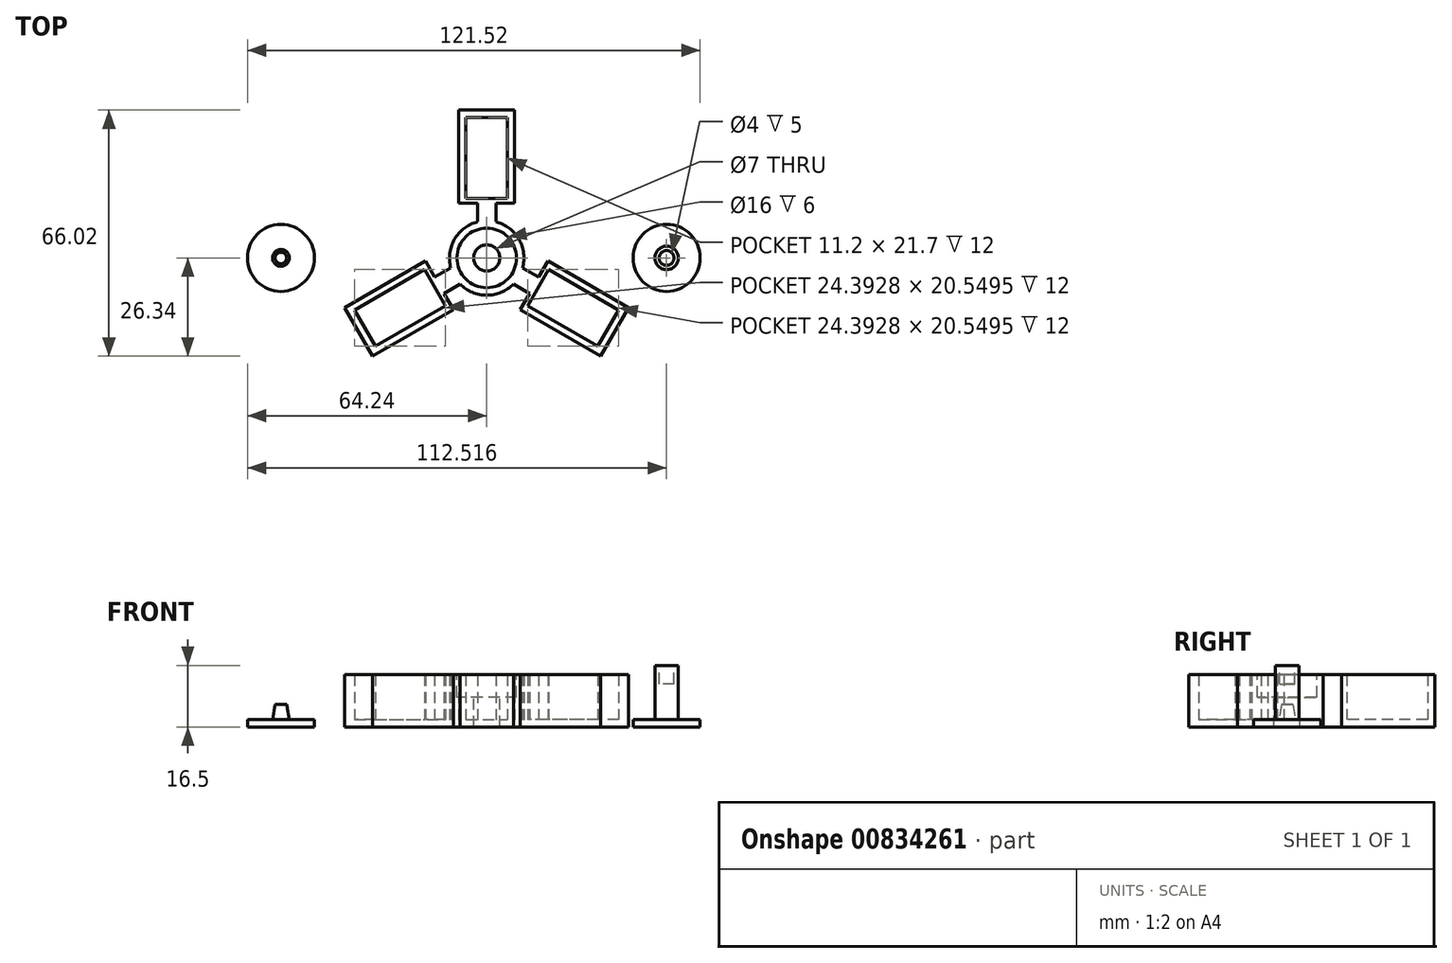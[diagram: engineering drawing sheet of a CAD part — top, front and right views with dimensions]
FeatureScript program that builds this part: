
annotation { "Feature Type Name" : "Feature", "Feature Type Description" : "" }
export const myFeature = defineFeature(function(context is Context, id is Id, definition is map)
    precondition{}
    {
        {
            var Q0;
            Q0=qCreatedBy(makeId("Top.planeOp"),FACE);
            var sketch = newSketch(context, id + "F0", { "sketchPlane" : qUnion([Q0])});
            skCircle(sketch, "E0", {"center": v(0, 0) * mm, "radius": 10 * mm});
            skPoint(sketch, "E1", {"position": v(-2.5, 9.68) * mm});
            skPoint(sketch, "E2", {"position": v(2.5, 9.68) * mm});
            skLineSegment(sketch, "E3", {"start": v(0, 24.16) * mm, "end": v(0, -23.06) * mm, "construction": true});
            skLineSegment(sketch, "E4", {"start": v(-2.5, 9.68) * mm, "end": v(-2.5, 14.68) * mm});
            skLineSegment(sketch, "E5", {"start": v(-2.5, 14.68) * mm, "end": v(2.5, 14.68) * mm});
            skLineSegment(sketch, "E6", {"start": v(2.5, 14.68) * mm, "end": v(2.5, 9.68) * mm});
            skLineSegment(sketch, "E7.bottom", {"start": v(-7.5, 14.68) * mm, "end": v(7.5, 14.68) * mm});
            skLineSegment(sketch, "E7.top", {"start": v(-7.5, 39.68) * mm, "end": v(7.5, 39.68) * mm});
            skLineSegment(sketch, "E7.left", {"start": v(-7.5, 14.68) * mm, "end": v(-7.5, 39.68) * mm});
            skLineSegment(sketch, "E7.right", {"start": v(7.5, 14.68) * mm, "end": v(7.5, 39.68) * mm});
            skLineSegment(sketch, "E8.1.0", {"start": v(-8.97, -13.84) * mm, "end": v(-30.62, -26.34) * mm});
            skLineSegment(sketch, "E8.1.1", {"start": v(-20.93, -12.08) * mm, "end": v(19.97, 11.53) * mm, "construction": true});
            skLineSegment(sketch, "E8.1.2", {"start": v(-16.47, -0.85) * mm, "end": v(-38.12, -13.35) * mm});
            skLineSegment(sketch, "E8.1.3", {"start": v(-7.14, -7) * mm, "end": v(-11.47, -9.5) * mm});
            skLineSegment(sketch, "E8.1.4", {"start": v(-13.97, -5.18) * mm, "end": v(-9.64, -2.68) * mm});
            skLineSegment(sketch, "E8.1.5", {"start": v(-8.97, -13.84) * mm, "end": v(-16.47, -0.85) * mm});
            skLineSegment(sketch, "E8.1.6", {"start": v(-30.62, -26.34) * mm, "end": v(-38.12, -13.35) * mm});
            skLineSegment(sketch, "E8.1.7", {"start": v(-11.47, -9.5) * mm, "end": v(-13.97, -5.18) * mm});
            skLineSegment(sketch, "E8.2.0", {"start": v(16.47, -0.85) * mm, "end": v(38.12, -13.35) * mm});
            skLineSegment(sketch, "E8.2.1", {"start": v(20.93, -12.08) * mm, "end": v(-19.97, 11.53) * mm, "construction": true});
            skLineSegment(sketch, "E8.2.2", {"start": v(8.97, -13.84) * mm, "end": v(30.62, -26.34) * mm});
            skLineSegment(sketch, "E8.2.3", {"start": v(9.64, -2.68) * mm, "end": v(13.97, -5.18) * mm});
            skLineSegment(sketch, "E8.2.4", {"start": v(11.47, -9.5) * mm, "end": v(7.14, -7) * mm});
            skLineSegment(sketch, "E8.2.5", {"start": v(16.47, -0.85) * mm, "end": v(8.97, -13.84) * mm});
            skLineSegment(sketch, "E8.2.6", {"start": v(38.12, -13.35) * mm, "end": v(30.62, -26.34) * mm});
            skLineSegment(sketch, "E8.2.7", {"start": v(13.97, -5.18) * mm, "end": v(11.47, -9.5) * mm});
            skSolve(sketch);
        }
        {
            var Q0;
            Q0 = qSketchRegion(id + "F0", true);
            extrude(context, id + "F1", {"entities" : qUnion([Q0]), "depth" : 2 * mm, "offsetDistance" : 25 * mm});
        }
        {
            var Q0;
            Q0=makeQuery(id+"F1.opExtrude","CAP_FACE",FACE,{"disambiguationData":[OSD([sQuery(id+"F0.wireOp",EDGE,"E0"),sQuery(id+"F0.wireOp",EDGE,"E4"),sQuery(id+"F0.wireOp",EDGE,"E6"),sQuery(id+"F0.wireOp",EDGE,"E7.bottom"),sQuery(id+"F0.wireOp",EDGE,"E7.top"),sQuery(id+"F0.wireOp",EDGE,"E7.left"),sQuery(id+"F0.wireOp",EDGE,"E7.right"),sQuery(id+"F0.wireOp",EDGE,"E8.1.0"),sQuery(id+"F0.wireOp",EDGE,"E8.1.2"),sQuery(id+"F0.wireOp",EDGE,"E8.1.3"),sQuery(id+"F0.wireOp",EDGE,"E8.1.4"),sQuery(id+"F0.wireOp",EDGE,"E8.1.5"),sQuery(id+"F0.wireOp",EDGE,"E8.1.6"),sQuery(id+"F0.wireOp",EDGE,"E8.2.0"),sQuery(id+"F0.wireOp",EDGE,"E8.2.2"),sQuery(id+"F0.wireOp",EDGE,"E8.2.3"),sQuery(id+"F0.wireOp",EDGE,"E8.2.4"),sQuery(id+"F0.wireOp",EDGE,"E8.2.5"),sQuery(id+"F0.wireOp",EDGE,"E8.2.6")])],"isStart":false});
            var sketch = newSketch(context, id + "F2", { "sketchPlane" : qUnion([Q0])});
            skLineSegment(sketch, "E9", {"start": v(0, -5.79) * mm, "end": v(0, 41.24) * mm, "construction": true});
            skPoint(sketch, "E9.endSnap0", {"position": v(0, 39.68) * mm});
            skLineSegment(sketch, "E10.bottom", {"start": v(-5.6, 37.68) * mm, "end": v(5.6, 37.68) * mm});
            skLineSegment(sketch, "E10.top", {"start": v(-5.6, 15.98) * mm, "end": v(5.6, 15.98) * mm});
            skLineSegment(sketch, "E10.left", {"start": v(-5.6, 37.68) * mm, "end": v(-5.6, 15.98) * mm});
            skLineSegment(sketch, "E10.right", {"start": v(5.6, 37.68) * mm, "end": v(5.6, 15.98) * mm});
            skPoint(sketch, "E11.1.0", {"position": v(-34.37, -19.84) * mm});
            skLineSegment(sketch, "E11.1.1", {"start": v(-35.43, -14) * mm, "end": v(-16.64, -3.14) * mm});
            skLineSegment(sketch, "E11.1.2", {"start": v(-29.83, -23.7) * mm, "end": v(-11.04, -12.84) * mm});
            skLineSegment(sketch, "E11.1.3", {"start": v(-11.04, -12.84) * mm, "end": v(-16.64, -3.14) * mm});
            skLineSegment(sketch, "E11.1.4", {"start": v(-29.83, -23.7) * mm, "end": v(-35.43, -14) * mm});
            skPoint(sketch, "E11.2.0", {"position": v(34.37, -19.84) * mm});
            skLineSegment(sketch, "E11.2.1", {"start": v(29.83, -23.7) * mm, "end": v(11.04, -12.84) * mm});
            skLineSegment(sketch, "E11.2.2", {"start": v(35.43, -14) * mm, "end": v(16.64, -3.14) * mm});
            skLineSegment(sketch, "E11.2.3", {"start": v(16.64, -3.14) * mm, "end": v(11.04, -12.84) * mm});
            skLineSegment(sketch, "E11.2.4", {"start": v(35.43, -14) * mm, "end": v(29.83, -23.7) * mm});
            skPoint(sketch, "E11.center", {"position": v(0, 0) * mm});
            skSolve(sketch);
        }
        {
            var Q0;
            Q0=makeQuery(id+"F2.imprint","IMPRINT",FACE,{"disambiguationData":[TD([[makeQuery(id+"F2.imprint","IMPRINT",EDGE,{"derivedFrom":sQuery(id+"F2.wireOp",EDGE,"E10.bottom")}),1.0]])]});
            extrude(context, id + "F3", {"entities" : qUnion([Q0]), "operationType" : NewBodyOperationType.ADD, "depth" : 12 * mm, "offsetDistance" : 25 * mm});
        }
        {
            var Q0;
            Q0=makeQuery(id+"F3.opExtrude","CAP_FACE",FACE,{"disambiguationData":[OSD([sQuery(id+"F0.wireOp",EDGE,"E0"),sQuery(id+"F0.wireOp",EDGE,"E4"),sQuery(id+"F0.wireOp",EDGE,"E6"),sQuery(id+"F0.wireOp",EDGE,"E7.bottom"),sQuery(id+"F0.wireOp",EDGE,"E7.top"),sQuery(id+"F0.wireOp",EDGE,"E7.left"),sQuery(id+"F0.wireOp",EDGE,"E7.right"),sQuery(id+"F0.wireOp",EDGE,"E8.1.0"),sQuery(id+"F0.wireOp",EDGE,"E8.1.2"),sQuery(id+"F0.wireOp",EDGE,"E8.1.3"),sQuery(id+"F0.wireOp",EDGE,"E8.1.4"),sQuery(id+"F0.wireOp",EDGE,"E8.1.5"),sQuery(id+"F0.wireOp",EDGE,"E8.1.6"),sQuery(id+"F0.wireOp",EDGE,"E8.2.0"),sQuery(id+"F0.wireOp",EDGE,"E8.2.2"),sQuery(id+"F0.wireOp",EDGE,"E8.2.3"),sQuery(id+"F0.wireOp",EDGE,"E8.2.4"),sQuery(id+"F0.wireOp",EDGE,"E8.2.5"),sQuery(id+"F0.wireOp",EDGE,"E8.2.6"),sQuery(id+"F2.wireOp",EDGE,"E10.bottom"),sQuery(id+"F2.wireOp",EDGE,"E10.top"),sQuery(id+"F2.wireOp",EDGE,"E10.left"),sQuery(id+"F2.wireOp",EDGE,"E10.right"),sQuery(id+"F2.wireOp",EDGE,"E11.1.1"),sQuery(id+"F2.wireOp",EDGE,"E11.1.2"),sQuery(id+"F2.wireOp",EDGE,"E11.1.3"),sQuery(id+"F2.wireOp",EDGE,"E11.1.4"),sQuery(id+"F2.wireOp",EDGE,"E11.2.1"),sQuery(id+"F2.wireOp",EDGE,"E11.2.2"),sQuery(id+"F2.wireOp",EDGE,"E11.2.3"),sQuery(id+"F2.wireOp",EDGE,"E11.2.4")])],"isStart":false});
            var sketch = newSketch(context, id + "F4", { "sketchPlane" : qUnion([Q0])});
            skCircle(sketch, "E12", {"center": v(0, 0) * mm, "radius": 3.5 * mm});
            skSolve(sketch);
        }
        {
            var Q0;
            Q0 = qSketchRegion(id + "F4", true);
            extrude(context, id + "F5", {"entities" : qUnion([Q0]), "operationType" : NewBodyOperationType.REMOVE, "oppositeDirection" : true, "depth" : 25 * mm, "offsetDistance" : 25 * mm});
        }
        {
            var Q0;
            Q0=makeQuery(id+"F3.opExtrude","CAP_FACE",FACE,{"disambiguationData":[OSD([sQuery(id+"F0.wireOp",EDGE,"E0"),sQuery(id+"F0.wireOp",EDGE,"E4"),sQuery(id+"F0.wireOp",EDGE,"E6"),sQuery(id+"F0.wireOp",EDGE,"E7.bottom"),sQuery(id+"F0.wireOp",EDGE,"E7.top"),sQuery(id+"F0.wireOp",EDGE,"E7.left"),sQuery(id+"F0.wireOp",EDGE,"E7.right"),sQuery(id+"F0.wireOp",EDGE,"E8.1.0"),sQuery(id+"F0.wireOp",EDGE,"E8.1.2"),sQuery(id+"F0.wireOp",EDGE,"E8.1.3"),sQuery(id+"F0.wireOp",EDGE,"E8.1.4"),sQuery(id+"F0.wireOp",EDGE,"E8.1.5"),sQuery(id+"F0.wireOp",EDGE,"E8.1.6"),sQuery(id+"F0.wireOp",EDGE,"E8.2.0"),sQuery(id+"F0.wireOp",EDGE,"E8.2.2"),sQuery(id+"F0.wireOp",EDGE,"E8.2.3"),sQuery(id+"F0.wireOp",EDGE,"E8.2.4"),sQuery(id+"F0.wireOp",EDGE,"E8.2.5"),sQuery(id+"F0.wireOp",EDGE,"E8.2.6"),sQuery(id+"F2.wireOp",EDGE,"E10.bottom"),sQuery(id+"F2.wireOp",EDGE,"E10.top"),sQuery(id+"F2.wireOp",EDGE,"E10.left"),sQuery(id+"F2.wireOp",EDGE,"E10.right"),sQuery(id+"F2.wireOp",EDGE,"E11.1.1"),sQuery(id+"F2.wireOp",EDGE,"E11.1.2"),sQuery(id+"F2.wireOp",EDGE,"E11.1.3"),sQuery(id+"F2.wireOp",EDGE,"E11.1.4"),sQuery(id+"F2.wireOp",EDGE,"E11.2.1"),sQuery(id+"F2.wireOp",EDGE,"E11.2.2"),sQuery(id+"F2.wireOp",EDGE,"E11.2.3"),sQuery(id+"F2.wireOp",EDGE,"E11.2.4")])],"isStart":false});
            var sketch = newSketch(context, id + "F6", { "sketchPlane" : qUnion([Q0])});
            skCircle(sketch, "E13", {"center": v(0, 0) * mm, "radius": 8 * mm});
            skSolve(sketch);
        }
        {
            var Q0;
            Q0 = qSketchRegion(id + "F6", true);
            extrude(context, id + "F7", {"entities" : qUnion([Q0]), "operationType" : NewBodyOperationType.REMOVE, "oppositeDirection" : true, "depth" : 6 * mm, "offsetDistance" : 25 * mm});
        }
        {
            var Q0;
            Q0=qCreatedBy(makeId("Top.planeOp"),FACE);
            var sketch = newSketch(context, id + "F8", { "sketchPlane" : qUnion([Q0])});
            skCircle(sketch, "E14", {"center": v(48.28, 0) * mm, "radius": 9 * mm});
            skSolve(sketch);
        }
        {
            var Q0;
            Q0=makeQuery(id+"F8.imprint","IMPRINT",FACE,{"disambiguationData":[TD([[makeQuery(id+"F8.imprint","IMPRINT",EDGE,{"derivedFrom":sQuery(id+"F8.wireOp",EDGE,"E14")}),1.0]])]});
            extrude(context, id + "F9", {"entities" : qUnion([Q0]), "depth" : 2 * mm, "offsetDistance" : 25 * mm});
        }
        {
            var Q0;
            Q0=makeQuery(id+"F9.opExtrude","CAP_FACE",FACE,{"disambiguationData":[OSD([sQuery(id+"F8.wireOp",EDGE,"E14")])],"isStart":false});
            var sketch = newSketch(context, id + "F10", { "sketchPlane" : qUnion([Q0])});
            skCircle(sketch, "E15", {"center": v(48.28, 0) * mm, "radius": 3.15 * mm});
            skSolve(sketch);
        }
        {
            var Q0;
            Q0 = qSketchRegion(id + "F10", true);
            extrude(context, id + "F11", {"entities" : qUnion([Q0]), "operationType" : NewBodyOperationType.ADD, "depth" : 14.5 * mm, "offsetDistance" : 25 * mm});
        }
        {
            var Q0;
            Q0=makeQuery(id+"F11.opExtrude","CAP_FACE",FACE,{"disambiguationData":[OSD([sQuery(id+"F10.wireOp",EDGE,"E15")])],"isStart":false});
            var sketch = newSketch(context, id + "F12", { "sketchPlane" : qUnion([Q0])});
            skCircle(sketch, "E16", {"center": v(48.28, 0) * mm, "radius": 2 * mm});
            skSolve(sketch);
        }
        {
            var Q0;
            Q0 = qSketchRegion(id + "F12", true);
            extrude(context, id + "F13", {"entities" : qUnion([Q0]), "operationType" : NewBodyOperationType.REMOVE, "oppositeDirection" : true, "depth" : 5 * mm, "offsetDistance" : 25 * mm});
        }
        {
            var Q0;
            Q0=qCreatedBy(makeId("Top.planeOp"),FACE);
            var sketch = newSketch(context, id + "F14", { "sketchPlane" : qUnion([Q0])});
            skCircle(sketch, "E17", {"center": v(-55.24, 0) * mm, "radius": 9 * mm});
            skSolve(sketch);
        }
        {
            var Q0;
            Q0 = qSketchRegion(id + "F14", true);
            extrude(context, id + "F15", {"entities" : qUnion([Q0]), "depth" : 2 * mm, "offsetDistance" : 25 * mm});
        }
        {
            var Q0;
            Q0=makeQuery(id+"F15.opExtrude","CAP_FACE",FACE,{"disambiguationData":[OSD([sQuery(id+"F14.wireOp",EDGE,"E17")])],"isStart":false});
            var sketch = newSketch(context, id + "F16", { "sketchPlane" : qUnion([Q0])});
            skCircle(sketch, "E18", {"center": v(-55.24, 0) * mm, "radius": 2.25 * mm});
            skSolve(sketch);
        }
        {
            var Q0;
            Q0 = qSketchRegion(id + "F16", true);
            extrude(context, id + "F17", {"entities" : qUnion([Q0]), "operationType" : NewBodyOperationType.ADD, "depth" : 4 * mm, "offsetDistance" : 25 * mm, "hasDraft" : true, "draftAngle" : 10 * degree, "draftPullDirection" : true});
        }
    });
